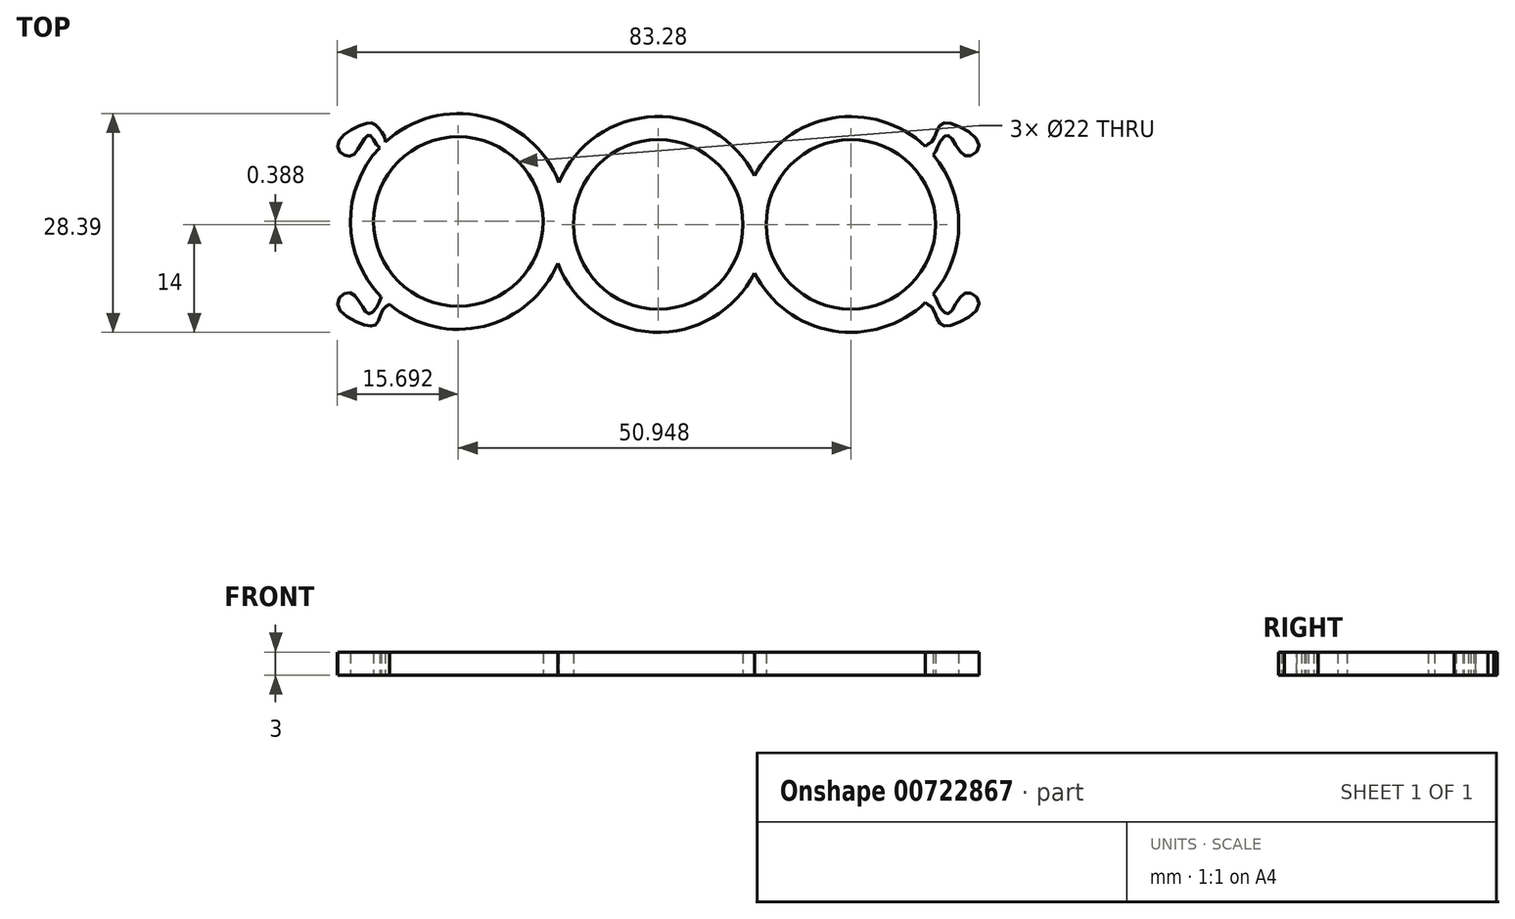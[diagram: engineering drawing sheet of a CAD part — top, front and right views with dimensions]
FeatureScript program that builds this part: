
annotation { "Feature Type Name" : "Feature", "Feature Type Description" : "" }
export const myFeature = defineFeature(function(context is Context, id is Id, definition is map)
    precondition{}
    {
        {
            var Q0;
            Q0=qCreatedBy(makeId("Top.planeOp"),FACE);
            var sketch = newSketch(context, id + "F0", { "sketchPlane" : qUnion([Q0])});
            skArc(sketch, "E0", {"start": v(0, 11) * mm, "mid": v(-11, 0) * mm, "end": v(0, -11) * mm});
            skArc(sketch, "E1", {"start": v(-13.05, -5.06) * mm, "mid": v(-7.9, -11.55) * mm, "end": v(0, -14) * mm});
            skCircle(sketch, "E2", {"center": v(-25.95, 0.39) * mm, "radius": 11 * mm});
            skArc(sketch, "E3", {"start": v(-12.9, 5.45) * mm, "mid": v(-22.79, 14.03) * mm, "end": v(-35.44, 10.68) * mm});
            skArc(sketch, "E4.trimOffspring", {"start": v(0, 14) * mm, "mid": v(-7.74, 11.67) * mm, "end": v(-12.9, 5.45) * mm});
            skArc(sketch, "E5.MirrorCS", {"start": v(12.5, 6.3) * mm, "mid": v(22.63, 13.8) * mm, "end": v(34.68, 10.11) * mm});
            skCircle(sketch, "E6.MirrorC", {"center": v(25, 0) * mm, "radius": 11 * mm});
            skArc(sketch, "E7.MirrorCS", {"start": v(12.5, -6.3) * mm, "mid": v(7.34, -11.92) * mm, "end": v(0, -14) * mm});
            skArc(sketch, "E8.MirrorCS", {"start": v(0, 11) * mm, "mid": v(11, 0) * mm, "end": v(0, -11) * mm});
            skArc(sketch, "E9.MirrorCS", {"start": v(0, 14) * mm, "mid": v(7.34, 11.92) * mm, "end": v(12.5, 6.3) * mm});
            skFitSpline(sketch, "E10", {"points": [v(-35.44, 10.68) * mm, v(-36.42, 12.67) * mm, v(-37.8, 13.13) * mm, v(-41.62, 10.44) * mm, v(-40.15, 8.84) * mm, v(-38.38, 10.7) * mm, v(-37.4, 11.59) * mm, v(-36.17, 9.96) * mm, v(-35.44, 10.68) * mm]});
            skArc(sketch, "E11.trimOffspring", {"start": v(-36.17, 9.96) * mm, "mid": v(-39.95, 0.25) * mm, "end": v(-35.98, -9.38) * mm});
            skFitSpline(sketch, "E12.MirrorC", {"points": [v(-35.44, -10.68) * mm, v(-36.42, -12.67) * mm, v(-37.8, -13.13) * mm, v(-41.62, -10.44) * mm, v(-40.15, -8.84) * mm, v(-38.38, -10.7) * mm, v(-37.4, -11.59) * mm, v(-36.17, -9.96) * mm, v(-35.67, -9.04) * mm, v(-34.75, -10.25) * mm, v(-35.44, -10.68) * mm]});
            skFitSpline(sketch, "E13.MirrorC", {"points": [v(35.44, 10.68) * mm, v(36.42, 12.67) * mm, v(37.8, 13.13) * mm, v(41.62, 10.44) * mm, v(40.15, 8.84) * mm, v(38.38, 10.7) * mm, v(37.4, 11.59) * mm, v(36.17, 9.96) * mm, v(35.67, 9.04) * mm, v(34.82, 9) * mm, v(34.75, 10.25) * mm, v(35.44, 10.68) * mm]});
            skFitSpline(sketch, "E14.MirrorC", {"points": [v(35.44, -10.68) * mm, v(36.42, -12.67) * mm, v(37.8, -13.13) * mm, v(41.62, -10.44) * mm, v(40.15, -8.84) * mm, v(38.38, -10.7) * mm, v(37.4, -11.59) * mm, v(36.17, -9.96) * mm, v(35.67, -9.04) * mm, v(34.82, -9) * mm, v(34.75, -10.25) * mm, v(35.44, -10.68) * mm]});
            skArc(sketch, "E15.trimOffspring", {"start": v(-34.86, -10.4) * mm, "mid": v(-22.62, -13.2) * mm, "end": v(-13.05, -5.06) * mm});
            skArc(sketch, "E16.trimOffspring", {"start": v(34.68, -10.11) * mm, "mid": v(22.63, -13.8) * mm, "end": v(12.5, -6.3) * mm});
            skArc(sketch, "E17.trimOffspring", {"start": v(35.68, 9.05) * mm, "mid": v(39, 0) * mm, "end": v(35.68, -9.05) * mm});
            skSolve(sketch);
        }
        {
            var Q0;
            Q0 = qSketchRegion(id + "F0", true);
            extrude(context, id + "F1", {"entities" : qUnion([Q0]), "depth" : 3 * mm, "offsetDistance" : 25 * mm});
        }
    });
